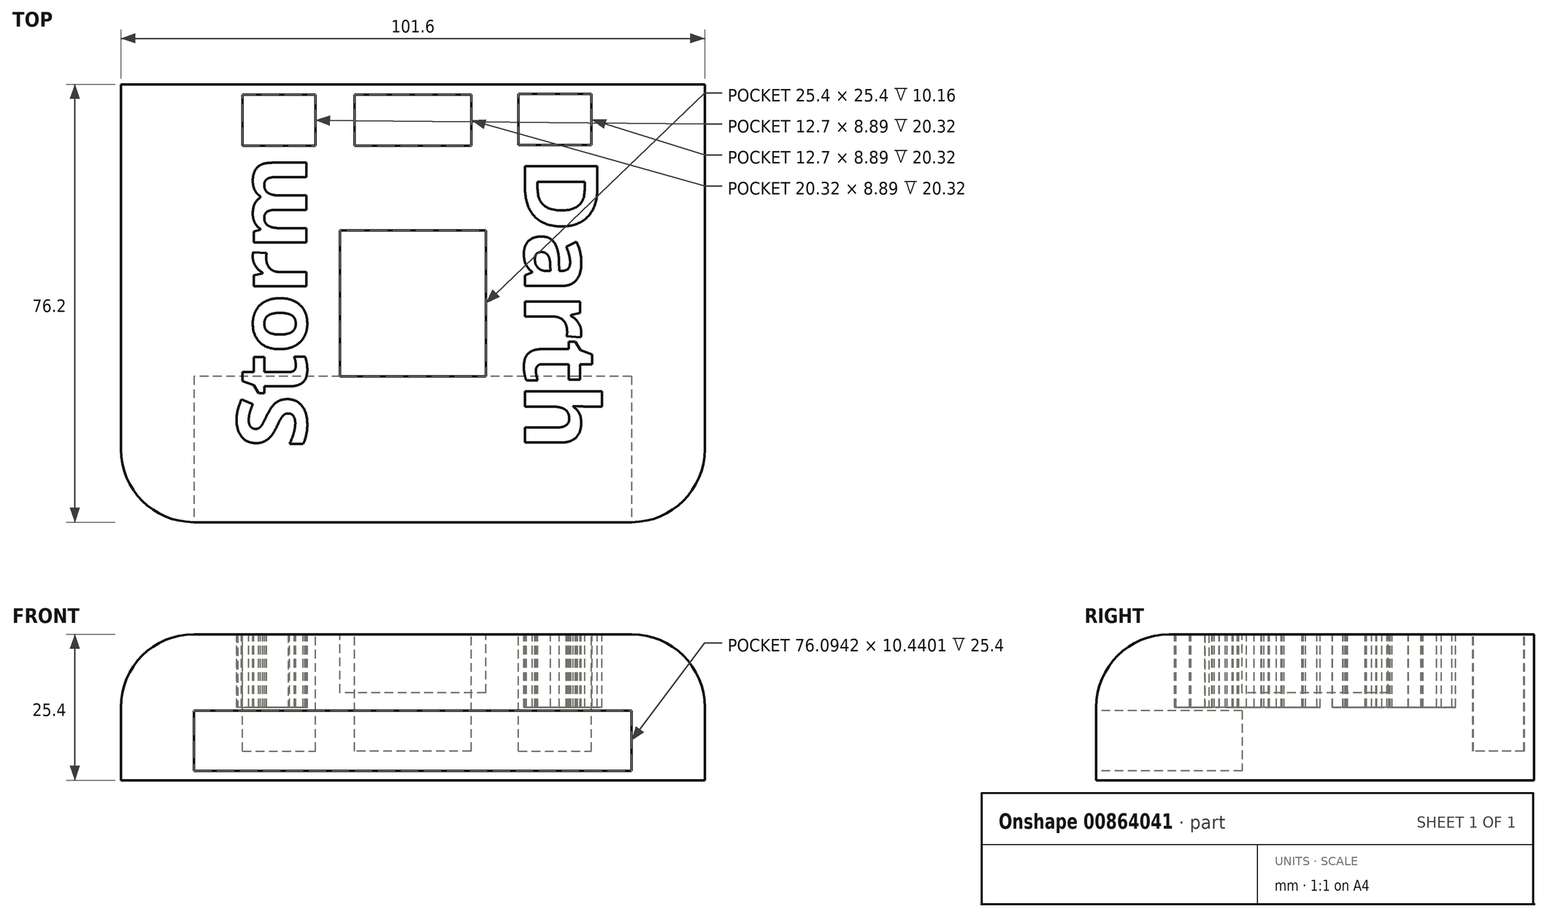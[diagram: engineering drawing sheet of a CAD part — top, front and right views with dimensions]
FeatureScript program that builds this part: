
annotation { "Feature Type Name" : "Feature", "Feature Type Description" : "" }
export const myFeature = defineFeature(function(context is Context, id is Id, definition is map)
    precondition{}
    {
        {
            var Q0;
            Q0=qCreatedBy(makeId("Top.planeOp"),FACE);
            var sketch = newSketch(context, id + "F0", { "sketchPlane" : qUnion([Q0])});
            skLineSegment(sketch, "E0.bottom", {"start": v(50.8, 38.1) * mm, "end": v(-50.8, 38.1) * mm});
            skLineSegment(sketch, "E0.top", {"start": v(50.8, -38.1) * mm, "end": v(-50.8, -38.1) * mm});
            skLineSegment(sketch, "E0.left", {"start": v(50.8, 38.1) * mm, "end": v(50.8, -38.1) * mm});
            skLineSegment(sketch, "E0.right", {"start": v(-50.8, 38.1) * mm, "end": v(-50.8, -38.1) * mm});
            skPoint(sketch, "E0.middle", {"position": v(0, 0) * mm});
            skSolve(sketch);
        }
        {
            var Q0;
            Q0=makeQuery(id+"F0.imprint","IMPRINT",FACE,{"disambiguationData":[TD([[makeQuery(id+"F0.imprint","IMPRINT",EDGE,{"derivedFrom":sQuery(id+"F0.wireOp",EDGE,"E0.bottom")}),1.0]])]});
            extrude(context, id + "F1", {"entities" : qUnion([Q0]), "depth" : 25.4 * mm, "offsetDistance" : 25.4 * mm});
        }
        {
            var Q0;
            Q0=makeQuery(id+"F1.opExtrude","SWEPT_EDGE",EDGE,{"disambiguationData":[OSD([sQuery(id+"F0.wireOp",EDGE,"E0.top"),sQuery(id+"F0.wireOp",EDGE,"E0.right")])]});
            var Q1;
            Q1=makeQuery(id+"F1.opExtrude","CAP_EDGE",EDGE,{"disambiguationData":[OSD([sQuery(id+"F0.wireOp",EDGE,"E0.top")])],"isStart":false});
            var Q2;
            Q2=makeQuery(id+"F1.opExtrude","SWEPT_EDGE",EDGE,{"disambiguationData":[OSD([sQuery(id+"F0.wireOp",EDGE,"E0.top"),sQuery(id+"F0.wireOp",EDGE,"E0.left")])]});
            var Q3;
            Q3=makeQuery(id+"F1.opExtrude","CAP_EDGE",EDGE,{"disambiguationData":[OSD([sQuery(id+"F0.wireOp",EDGE,"E0.left")])],"isStart":false});
            var Q4;
            Q4=makeQuery(id+"F1.opExtrude","CAP_EDGE",EDGE,{"disambiguationData":[OSD([sQuery(id+"F0.wireOp",EDGE,"E0.right")])],"isStart":false});
            fillet(context, id + "F2", {"entities" : qUnion([Q0, Q1, Q2, Q3, Q4]), "radius" : 12.7 * mm, "tangentPropagation" : true, "allowEdgeOverflow" : false});
        }
        {
            var Q0;
            Q0=makeQuery(id+"F1.opExtrude","CAP_FACE",FACE,{"disambiguationData":[OSD([sQuery(id+"F0.wireOp",EDGE,"E0.bottom"),sQuery(id+"F0.wireOp",EDGE,"E0.top"),sQuery(id+"F0.wireOp",EDGE,"E0.left"),sQuery(id+"F0.wireOp",EDGE,"E0.right")])],"isStart":false});
            var sketch = newSketch(context, id + "F3", { "sketchPlane" : qUnion([Q0])});
            skLineSegment(sketch, "E1.bottom", {"start": v(12.7, 12.7) * mm, "end": v(-12.7, 12.7) * mm});
            skLineSegment(sketch, "E1.top", {"start": v(12.7, -12.7) * mm, "end": v(-12.7, -12.7) * mm});
            skLineSegment(sketch, "E1.left", {"start": v(12.7, 12.7) * mm, "end": v(12.7, -12.7) * mm});
            skLineSegment(sketch, "E1.right", {"start": v(-12.7, 12.7) * mm, "end": v(-12.7, -12.7) * mm});
            skPoint(sketch, "E1.middle", {"position": v(0, 0) * mm});
            skSolve(sketch);
        }
        {
            var Q0;
            Q0=makeQuery(id+"F3.imprint","IMPRINT",FACE,{"disambiguationData":[TD([[makeQuery(id+"F3.imprint","IMPRINT",EDGE,{"derivedFrom":sQuery(id+"F3.wireOp",EDGE,"E1.bottom")}),1.0]])]});
            extrude(context, id + "F4", {"entities" : qUnion([Q0]), "operationType" : NewBodyOperationType.REMOVE, "oppositeDirection" : true, "depth" : 10.16 * mm, "offsetDistance" : 25.4 * mm});
        }
        {
            var Q0;
            Q0=makeQuery(id+"F1.opExtrude","CAP_FACE",FACE,{"disambiguationData":[OSD([sQuery(id+"F0.wireOp",EDGE,"E0.bottom"),sQuery(id+"F0.wireOp",EDGE,"E0.top"),sQuery(id+"F0.wireOp",EDGE,"E0.left"),sQuery(id+"F0.wireOp",EDGE,"E0.right")])],"isStart":false});
            var sketch = newSketch(context, id + "F5", { "sketchPlane" : qUnion([Q0])});
            skText(sketch, "E2", { "text": "Darth", "fontName": "OpenSans-Bold.ttf"});
            const initialGuessF5  = {"E2": [0.0195, 0.0254, 0, -1, 0.0127]};
            skSetInitialGuess(sketch, initialGuessF5);
            skSolve(sketch);
        }
        {
            var Q0;
            Q0=makeQuery(id+"F5.imprint","IMPRINT",FACE,{"disambiguationData":[TD([[makeQuery(id+"F5.imprint","IMPRINT",EDGE,{"derivedFrom":sQuery(id+"F5.wireOp",EDGE,"E2.sketch_text.stroke-0")}),1.0]])]});
            var sketch = newSketch(context, id + "F6", { "sketchPlane" : qUnion([Q0])});
            skText(sketch, "E3", { "text": "Storm ", "fontName": "OpenSans-Bold.ttf"});
            const initialGuessF6  = {"E3": [-0.01852, -0.02526, 0, 1, 0.01207]};
            skSetInitialGuess(sketch, initialGuessF6);
            skSolve(sketch);
        }
        {
            var Q0;
            Q0 = qSketchRegion(id + "F6", true);
            var Q1;
            Q1 = qSketchRegion(id + "F5", true);
            extrude(context, id + "F7", {"entities" : qUnion([Q0, Q1]), "operationType" : NewBodyOperationType.REMOVE, "oppositeDirection" : true, "depth" : 12.7 * mm, "offsetDistance" : 25.4 * mm});
        }
        {
            var Q0;
            Q0=makeQuery(id+"F1.opExtrude","SWEPT_FACE",FACE,{"disambiguationData":[OSD([sQuery(id+"F0.wireOp",EDGE,"E0.top")])]});
            var sketch = newSketch(context, id + "F8", { "sketchPlane" : qUnion([Q0])});
            skLineSegment(sketch, "E4.bottom", {"start": v(38.05, 12.09) * mm, "end": v(-38.05, 12.09) * mm});
            skLineSegment(sketch, "E4.top", {"start": v(38.05, 1.65) * mm, "end": v(-38.05, 1.65) * mm});
            skLineSegment(sketch, "E4.left", {"start": v(38.05, 12.09) * mm, "end": v(38.05, 1.65) * mm});
            skLineSegment(sketch, "E4.right", {"start": v(-38.05, 12.09) * mm, "end": v(-38.05, 1.65) * mm});
            skPoint(sketch, "E4.middle", {"position": v(0, 6.87) * mm});
            skSolve(sketch);
        }
        {
            var Q0;
            Q0=makeQuery(id+"F8.imprint","IMPRINT",FACE,{"disambiguationData":[TD([[makeQuery(id+"F8.imprint","IMPRINT",EDGE,{"derivedFrom":sQuery(id+"F8.wireOp",EDGE,"E4.bottom")}),1.0]])]});
            extrude(context, id + "F9", {"entities" : qUnion([Q0]), "operationType" : NewBodyOperationType.REMOVE, "oppositeDirection" : true, "depth" : 25.4 * mm, "offsetDistance" : 25.4 * mm});
        }
        {
            var Q0;
            {var subQ0=sQuery(id+"F0.wireOp",EDGE,"E0.bottom");var subQ1=sQuery(id+"F0.wireOp",EDGE,"E0.top");var subQ2=sQuery(id+"F0.wireOp",EDGE,"E0.left");var subQ3=sQuery(id+"F0.wireOp",EDGE,"E0.right");Q0=makeQuery(id+"F7.boolean.opBoolean","SPLIT",FACE,{"disambiguationData":[TD([makeQuery(id+"F1.opExtrude","SWEPT_FACE",FACE,{"disambiguationData":[OSD([subQ0])]})])],"derivedFrom":makeQuery(id+"F1.opExtrude","CAP_FACE",FACE,{"disambiguationData":[OSD([subQ0,subQ1,subQ2,subQ3])],"isStart":false})});}
            var sketch = newSketch(context, id + "F10", { "sketchPlane" : qUnion([Q0])});
            skLineSegment(sketch, "E5.bottom", {"start": v(-29.62, 36.27) * mm, "end": v(-16.92, 36.27) * mm});
            skLineSegment(sketch, "E5.top", {"start": v(-29.62, 27.38) * mm, "end": v(-16.92, 27.38) * mm});
            skLineSegment(sketch, "E5.left", {"start": v(-29.62, 36.27) * mm, "end": v(-29.62, 27.38) * mm});
            skLineSegment(sketch, "E5.right", {"start": v(-16.92, 36.27) * mm, "end": v(-16.92, 27.38) * mm});
            skSolve(sketch);
        }
        {
            var Q0;
            Q0=makeQuery(id+"F10.imprint","IMPRINT",FACE,{"disambiguationData":[TD([[makeQuery(id+"F10.imprint","IMPRINT",EDGE,{"derivedFrom":sQuery(id+"F10.wireOp",EDGE,"E5.bottom")}),-1.0]])]});
            extrude(context, id + "F11", {"entities" : qUnion([Q0]), "operationType" : NewBodyOperationType.REMOVE, "oppositeDirection" : true, "depth" : 20.32 * mm, "offsetDistance" : 25.4 * mm});
        }
        {
            var Q0;
            {var subQ0=sQuery(id+"F0.wireOp",EDGE,"E0.bottom");var subQ1=sQuery(id+"F0.wireOp",EDGE,"E0.top");var subQ2=sQuery(id+"F0.wireOp",EDGE,"E0.left");var subQ3=sQuery(id+"F0.wireOp",EDGE,"E0.right");Q0=makeQuery(id+"F7.boolean.opBoolean","SPLIT",FACE,{"disambiguationData":[TD([makeQuery(id+"F1.opExtrude","SWEPT_FACE",FACE,{"disambiguationData":[OSD([subQ0])]})])],"derivedFrom":makeQuery(id+"F1.opExtrude","CAP_FACE",FACE,{"disambiguationData":[OSD([subQ0,subQ1,subQ2,subQ3])],"isStart":false})});}
            var sketch = newSketch(context, id + "F12", { "sketchPlane" : qUnion([Q0])});
            skLineSegment(sketch, "E6.bottom", {"start": v(10.16, 36.27) * mm, "end": v(-10.16, 36.27) * mm});
            skLineSegment(sketch, "E6.top", {"start": v(10.16, 27.38) * mm, "end": v(-10.16, 27.38) * mm});
            skLineSegment(sketch, "E6.left", {"start": v(10.16, 36.27) * mm, "end": v(10.16, 27.38) * mm});
            skLineSegment(sketch, "E6.right", {"start": v(-10.16, 36.27) * mm, "end": v(-10.16, 27.38) * mm});
            skPoint(sketch, "E6.middle", {"position": v(0, 31.82) * mm});
            skPoint(sketch, "E6.middle.positionSnap0", {"position": v(-16.92, 31.82) * mm});
            skPoint(sketch, "E6.centerSnap0", {"position": v(-16.92, 31.82) * mm});
            skSolve(sketch);
        }
        {
            var Q0;
            Q0=makeQuery(id+"F12.imprint","IMPRINT",FACE,{"disambiguationData":[TD([[makeQuery(id+"F12.imprint","IMPRINT",EDGE,{"derivedFrom":sQuery(id+"F12.wireOp",EDGE,"E6.bottom")}),-1.0]])]});
            var sketch = newSketch(context, id + "F13", { "sketchPlane" : qUnion([Q0])});
            skLineSegment(sketch, "E7.bottom", {"start": v(18.38, 36.4) * mm, "end": v(31.08, 36.4) * mm});
            skLineSegment(sketch, "E7.top", {"start": v(18.38, 27.52) * mm, "end": v(31.08, 27.52) * mm});
            skLineSegment(sketch, "E7.left", {"start": v(18.38, 36.4) * mm, "end": v(18.38, 27.52) * mm});
            skLineSegment(sketch, "E7.right", {"start": v(31.08, 36.4) * mm, "end": v(31.08, 27.52) * mm});
            skPoint(sketch, "E7.middle", {"position": v(24.73, 31.96) * mm});
            skSolve(sketch);
        }
        {
            var Q0;
            Q0=makeQuery(id+"F12.imprint","IMPRINT",FACE,{"disambiguationData":[TD([[makeQuery(id+"F12.imprint","IMPRINT",EDGE,{"derivedFrom":sQuery(id+"F12.wireOp",EDGE,"E6.bottom")}),1.0]])]});
            var Q1;
            Q1=makeQuery(id+"F13.imprint","IMPRINT",FACE,{"disambiguationData":[TD([[makeQuery(id+"F13.imprint","IMPRINT",EDGE,{"derivedFrom":sQuery(id+"F13.wireOp",EDGE,"E7.bottom")}),-1.0]])]});
            extrude(context, id + "F14", {"entities" : qUnion([Q0, Q1]), "operationType" : NewBodyOperationType.REMOVE, "oppositeDirection" : true, "depth" : 20.32 * mm, "offsetDistance" : 25.4 * mm});
        }
    });
